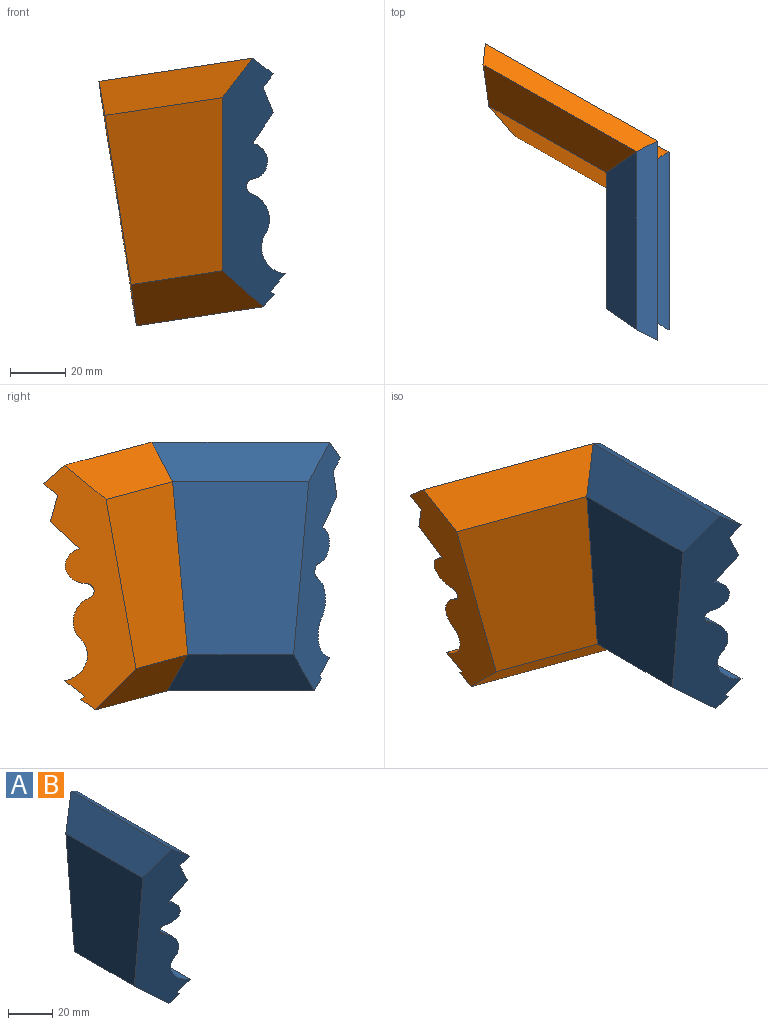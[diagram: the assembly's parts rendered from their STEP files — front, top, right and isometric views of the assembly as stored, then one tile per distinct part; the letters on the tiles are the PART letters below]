
ASSEMBLY  parts=2 mates=1
PART A: 16 faces, bbox 22.7x72.4x90.3 mm
  f0: plane 90.33x22.73mm, normal (-0.5,-0.86,-0.08), area 1428.3mm2, adj f2,f3,f4,f5,f6,f7,f8,f9
  f1: plane 90.33x22.73mm, normal (-0.5,0.86,-0.08), area 1428.3mm2, adj f2,f3,f4,f5,f6,f7,f8,f9
  f2: plane 53.33x14.79mm, normal (-0.66,0,-0.75), area 906.1mm2, adj f0,f1,f3,f15
  f3: plane 58.79x4.47mm, normal (0.74,0,-0.67), area 337.4mm2, adj f0,f1,f2,f4
  f4: plane 58.79x1.34mm, normal (0.63,0,0.78), area 100.4mm2, adj f0,f1,f3,f5
  f5: plane 64.64x6.45mm, normal (0.78,0,-0.63), area 507.4mm2, adj f0,f1,f4,f6
  f6: cylinder r=9.62mm len=64.64mm, axis (0,1,0), area 1183.8mm2, adj f0,f1,f5,f7
  f7: cylinder r=10.21mm len=61.62mm, axis (0,1,0), area 974.4mm2, adj f0,f1,f6,f8
  f8: cylinder r=2.79mm len=56.96mm, axis (0,1,0), area 417.1mm2, adj f0,f1,f7,f9
  f9: cylinder r=6.55mm len=64.52mm, axis (0,1,0), area 1143.1mm2, adj f0,f1,f8,f10
  f10: plane 69.92x11.2mm, normal (0.83,0,-0.56), area 872.1mm2, adj f0,f1,f9,f11
  f11: plane 69.92x9.26mm, normal (0.93,0,0.37), area 683.3mm2, adj f0,f1,f10,f12
  f12: plane 72.39x4.83mm, normal (0.8,0,-0.61), area 423.3mm2, adj f0,f1,f11,f13
  f13: plane 72.39x7.55mm, normal (0.61,0,0.8), area 649.3mm2, adj f0,f1,f12,f14
  f14: plane 64.64x14.36mm, normal (-0.8,0,0.61), area 1029.3mm2, adj f0,f1,f13,f15
  f15: plane 62.9x49.48mm, normal (-1,0,0), area 2766.3mm2, adj f0,f1,f2,f14
PART B: same geometry as A
PLACE A t=(-230.34,219.06,-20.63)mm
PLACE B rot(axis=(-0.15,0,0.99),60.8deg) t=(-253.34,258.76,-24.11)mm
MATE fastened B.f0 <-> A.f1  axis (0.5,-0.86,0.08) through (-226.67,255.25,63.96)mm
